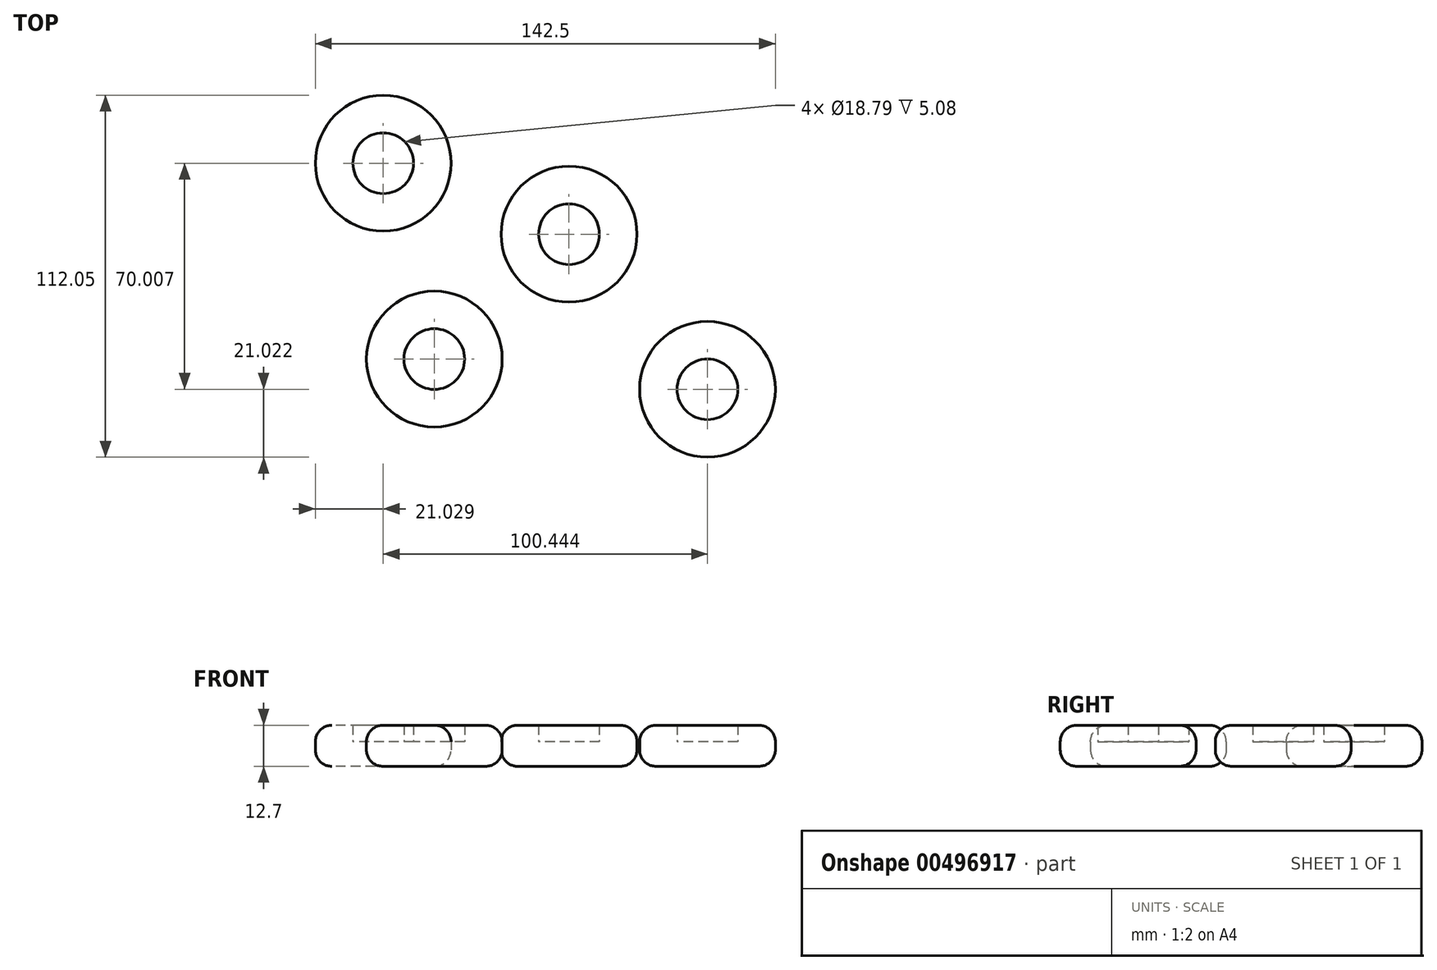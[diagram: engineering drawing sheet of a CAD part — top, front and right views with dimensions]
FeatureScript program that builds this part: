
annotation { "Feature Type Name" : "Feature", "Feature Type Description" : "" }
export const myFeature = defineFeature(function(context is Context, id is Id, definition is map)
    precondition{}
    {
        {
            var Q0;
            Q0=qCreatedBy(makeId("Top.planeOp"),FACE);
            var sketch = newSketch(context, id + "F0", { "sketchPlane" : qUnion([Q0])});
            skCircle(sketch, "E0", {"center": v(0, 0) * mm, "radius": 21.03 * mm});
            skCircle(sketch, "E1", {"center": v(0, 0) * mm, "radius": 9.4 * mm});
            skCircle(sketch, "E2", {"center": v(-57.56, 21.98) * mm, "radius": 21.03 * mm});
            skCircle(sketch, "E3", {"center": v(-57.56, 21.98) * mm, "radius": 9.4 * mm});
            skCircle(sketch, "E4", {"center": v(-41.73, -38.67) * mm, "radius": 21.03 * mm});
            skCircle(sketch, "E5", {"center": v(-41.73, -38.67) * mm, "radius": 9.4 * mm});
            skCircle(sketch, "E6", {"center": v(42.88, -48.03) * mm, "radius": 21.03 * mm});
            skCircle(sketch, "E7", {"center": v(42.88, -48.03) * mm, "radius": 9.4 * mm});
            skSolve(sketch);
        }
        {
            var Q0;
            Q0=makeQuery(id+"F0.imprint","IMPRINT",FACE,{"disambiguationData":[TD([[makeQuery(id+"F0.imprint","IMPRINT",EDGE,{"derivedFrom":sQuery(id+"F0.wireOp",EDGE,"E0")}),1.0]])]});
            extrude(context, id + "F1", {"entities" : qUnion([Q0]), "depth" : 12.7 * mm});
        }
        {
            var Q0;
            Q0=makeQuery(id+"F1.opExtrude","SWEPT_FACE",FACE,{"disambiguationData":[OSD([sQuery(id+"F0.wireOp",EDGE,"E0")])]});
            fillet(context, id + "F2", {"entities" : qUnion([Q0]), "radius" : 5.08 * mm, "tangentPropagation" : true, "allowEdgeOverflow" : false});
        }
        {
            var Q0;
            Q0=makeQuery(id+"F0.imprint","IMPRINT",FACE,{"disambiguationData":[TD([[makeQuery(id+"F0.imprint","IMPRINT",EDGE,{"derivedFrom":sQuery(id+"F0.wireOp",EDGE,"E1")}),1.0]])]});
            extrude(context, id + "F3", {"entities" : qUnion([Q0]), "operationType" : NewBodyOperationType.ADD, "depth" : 7.62 * mm});
        }
        {
            var Q0;
            Q0=makeQuery(id+"F0.imprint","IMPRINT",FACE,{"disambiguationData":[TD([[makeQuery(id+"F0.imprint","IMPRINT",EDGE,{"derivedFrom":sQuery(id+"F0.wireOp",EDGE,"E2")}),1.0]])]});
            extrude(context, id + "F4", {"entities" : qUnion([Q0]), "depth" : 25.4 * mm});
        }
        {
            var Q0;
            Q0=makeQuery(id+"F4.opExtrude","SWEPT_FACE",FACE,{"disambiguationData":[OSD([sQuery(id+"F0.wireOp",EDGE,"E2")])]});
            fillet(context, id + "F5", {"entities" : qUnion([Q0]), "radius" : 5.08 * mm, "tangentPropagation" : true, "allowEdgeOverflow" : false});
        }
        {
            var Q0;
            Q0=makeQuery(id+"F0.imprint","IMPRINT",FACE,{"disambiguationData":[TD([[makeQuery(id+"F0.imprint","IMPRINT",EDGE,{"derivedFrom":sQuery(id+"F0.wireOp",EDGE,"E3")}),1.0]])]});
            extrude(context, id + "F6", {"entities" : qUnion([Q0]), "operationType" : NewBodyOperationType.ADD, "depth" : 12.7 * mm});
        }
        {
            var Q0;
            Q0=makeQuery(id+"F0.imprint","IMPRINT",FACE,{"disambiguationData":[TD([[makeQuery(id+"F0.imprint","IMPRINT",EDGE,{"derivedFrom":sQuery(id+"F0.wireOp",EDGE,"E4")}),1.0]])]});
            extrude(context, id + "F7", {"entities" : qUnion([Q0]), "depth" : 25.4 * mm});
        }
        {
            var Q0;
            Q0=makeQuery(id+"F7.opExtrude","SWEPT_FACE",FACE,{"disambiguationData":[OSD([sQuery(id+"F0.wireOp",EDGE,"E4")])]});
            fillet(context, id + "F8", {"entities" : qUnion([Q0]), "radius" : 5.08 * mm, "tangentPropagation" : true, "allowEdgeOverflow" : false});
        }
        {
            var Q0;
            Q0=makeQuery(id+"F0.imprint","IMPRINT",FACE,{"disambiguationData":[TD([[makeQuery(id+"F0.imprint","IMPRINT",EDGE,{"derivedFrom":sQuery(id+"F0.wireOp",EDGE,"E5")}),1.0]])]});
            extrude(context, id + "F9", {"entities" : qUnion([Q0]), "operationType" : NewBodyOperationType.ADD, "depth" : 12.7 * mm});
        }
        {
            var Q0;
            Q0=makeQuery(id+"F0.imprint","IMPRINT",FACE,{"disambiguationData":[TD([[makeQuery(id+"F0.imprint","IMPRINT",EDGE,{"derivedFrom":sQuery(id+"F0.wireOp",EDGE,"E6")}),1.0]])]});
            extrude(context, id + "F10", {"entities" : qUnion([Q0]), "depth" : 25.4 * mm});
        }
        {
            var Q0;
            Q0=makeQuery(id+"F10.opExtrude","SWEPT_FACE",FACE,{"disambiguationData":[OSD([sQuery(id+"F0.wireOp",EDGE,"E6")])]});
            fillet(context, id + "F11", {"entities" : qUnion([Q0]), "radius" : 5.08 * mm, "tangentPropagation" : true, "allowEdgeOverflow" : false});
        }
        {
            var Q0;
            Q0=makeQuery(id+"F0.imprint","IMPRINT",FACE,{"disambiguationData":[TD([[makeQuery(id+"F0.imprint","IMPRINT",EDGE,{"derivedFrom":sQuery(id+"F0.wireOp",EDGE,"E7")}),1.0]])]});
            extrude(context, id + "F12", {"entities" : qUnion([Q0]), "operationType" : NewBodyOperationType.ADD, "depth" : 12.7 * mm});
        }
        {
            var Q0;
            Q0=makeQuery(id+"F4.opExtrude","SWEPT_BODY",BODY,{"disambiguationData":[OSD([sQuery(id+"F0.wireOp",EDGE,"E2"),sQuery(id+"F0.wireOp",EDGE,"E3")])]});
            deleteBodies(context, id + "F13", {"entities" : qUnion([Q0])});
        }
        {
            var Q0;
            Q0=makeQuery(id+"F7.opExtrude","SWEPT_BODY",BODY,{"disambiguationData":[OSD([sQuery(id+"F0.wireOp",EDGE,"E4"),sQuery(id+"F0.wireOp",EDGE,"E5")])]});
            deleteBodies(context, id + "F14", {"entities" : qUnion([Q0])});
        }
        {
            var Q0;
            Q0=makeQuery(id+"F10.opExtrude","SWEPT_BODY",BODY,{"disambiguationData":[OSD([sQuery(id+"F0.wireOp",EDGE,"E6"),sQuery(id+"F0.wireOp",EDGE,"E7")])]});
            deleteBodies(context, id + "F15", {"entities" : qUnion([Q0])});
        }
        {
            var Q0;
            Q0=makeQuery(id+"F0.imprint","IMPRINT",FACE,{"disambiguationData":[TD([[makeQuery(id+"F0.imprint","IMPRINT",EDGE,{"derivedFrom":sQuery(id+"F0.wireOp",EDGE,"E2")}),1.0]])]});
            extrude(context, id + "F16", {"entities" : qUnion([Q0]), "depth" : 12.7 * mm});
        }
        {
            var Q0;
            Q0=makeQuery(id+"F16.opExtrude","SWEPT_FACE",FACE,{"disambiguationData":[OSD([sQuery(id+"F0.wireOp",EDGE,"E2")])]});
            fillet(context, id + "F17", {"entities" : qUnion([Q0]), "radius" : 5.08 * mm, "tangentPropagation" : true, "allowEdgeOverflow" : false});
        }
        {
            var Q0;
            Q0=makeQuery(id+"F0.imprint","IMPRINT",FACE,{"disambiguationData":[TD([[makeQuery(id+"F0.imprint","IMPRINT",EDGE,{"derivedFrom":sQuery(id+"F0.wireOp",EDGE,"E3")}),1.0]])]});
            extrude(context, id + "F18", {"entities" : qUnion([Q0]), "operationType" : NewBodyOperationType.ADD, "depth" : 7.62 * mm});
        }
        {
            var Q0;
            Q0=makeQuery(id+"F0.imprint","IMPRINT",FACE,{"disambiguationData":[TD([[makeQuery(id+"F0.imprint","IMPRINT",EDGE,{"derivedFrom":sQuery(id+"F0.wireOp",EDGE,"E6")}),1.0]])]});
            extrude(context, id + "F19", {"entities" : qUnion([Q0]), "depth" : 12.7 * mm});
        }
        {
            var Q0;
            Q0=makeQuery(id+"F19.opExtrude","SWEPT_FACE",FACE,{"disambiguationData":[OSD([sQuery(id+"F0.wireOp",EDGE,"E6")])]});
            fillet(context, id + "F20", {"entities" : qUnion([Q0]), "radius" : 5.08 * mm, "tangentPropagation" : true, "allowEdgeOverflow" : false});
        }
        {
            var Q0;
            Q0=makeQuery(id+"F0.imprint","IMPRINT",FACE,{"disambiguationData":[TD([[makeQuery(id+"F0.imprint","IMPRINT",EDGE,{"derivedFrom":sQuery(id+"F0.wireOp",EDGE,"E4")}),1.0]])]});
            extrude(context, id + "F21", {"entities" : qUnion([Q0]), "depth" : 12.7 * mm});
        }
        {
            var Q0;
            Q0=makeQuery(id+"F21.opExtrude","SWEPT_FACE",FACE,{"disambiguationData":[OSD([sQuery(id+"F0.wireOp",EDGE,"E4")])]});
            fillet(context, id + "F22", {"entities" : qUnion([Q0]), "radius" : 5.08 * mm, "tangentPropagation" : true, "allowEdgeOverflow" : false});
        }
        {
            var Q0;
            Q0=makeQuery(id+"F0.imprint","IMPRINT",FACE,{"disambiguationData":[TD([[makeQuery(id+"F0.imprint","IMPRINT",EDGE,{"derivedFrom":sQuery(id+"F0.wireOp",EDGE,"E7")}),1.0]])]});
            extrude(context, id + "F23", {"entities" : qUnion([Q0]), "operationType" : NewBodyOperationType.ADD, "depth" : 7.62 * mm});
        }
        {
            var Q0;
            Q0=makeQuery(id+"F0.imprint","IMPRINT",FACE,{"disambiguationData":[TD([[makeQuery(id+"F0.imprint","IMPRINT",EDGE,{"derivedFrom":sQuery(id+"F0.wireOp",EDGE,"E5")}),1.0]])]});
            extrude(context, id + "F24", {"entities" : qUnion([Q0]), "operationType" : NewBodyOperationType.ADD, "depth" : 7.62 * mm});
        }
    });
